# Revit family: Legrand Cabinet XL³ 160 Metal
name_source: partatom
category: Equipement électrique
units: mm (PartAtom-declared; Revit-internal decimal feet)

## family parameters
Basée sur le plan de construction = Non
Configuration du panneau = Deux colonnes, circuits au sein
Cote de connecteur circulaire = Utiliser le diamètre
Couper avec des vides une fois chargée = Non
Numéro OmniClass = 23.80.30.11.17
Partagée = Non
Point de calcul de pièce = Non
Titre OmniClass = Distribution Boards and Control Panels
Toujours verticalement = Oui
Type d'élément = Tableau de raccordement

## types (5) — shared parameters
Fabricant = Legrand
Finish = Epoxipolyester paint deposited by electrostatic powder
General Conditions of Use = https://export.legrand.com
ICW (until) (kA) = 0
IK with door = 08
IK without door = 07
IN max (A) = 160
IP with door = 43
IP without door = 30
IPK (kA) = 35
Material = Steel
Material corner = Plastic
Modèle = XL³ 160 Metal
RAL = 7035
URL = https://www.legrand.fr
depth (mm) = 170 mm  [stored 0.557743 ft]
depth installation zone = 720 mm  [stored 2.3622 ft]
width (mm) = 575 mm
width installation zone = 1245 mm
zero-valued in all types: Elévation par défaut

## per-type parameters (varying)
| type | height (mm) | height installation zone |
| 020003-020273 | 600 mm | 600 mm |
| 020002-020272 | 450 mm  [stored 1.47638 ft] | 450 mm  [stored 1.47638 ft] |
| 020004-020274 | 750 mm  [stored 2.46063 ft] | 750 mm  [stored 2.46063 ft] |
| 020005-020275 | 900 mm  [stored 2.95276 ft] | 900 mm  [stored 2.95276 ft] |
| 020006-020276 | 1050 mm | 1050 mm |

note: [stored X ft] marks values corroborated as IEEE doubles in the binary element streams (Revit-internal decimal feet)
